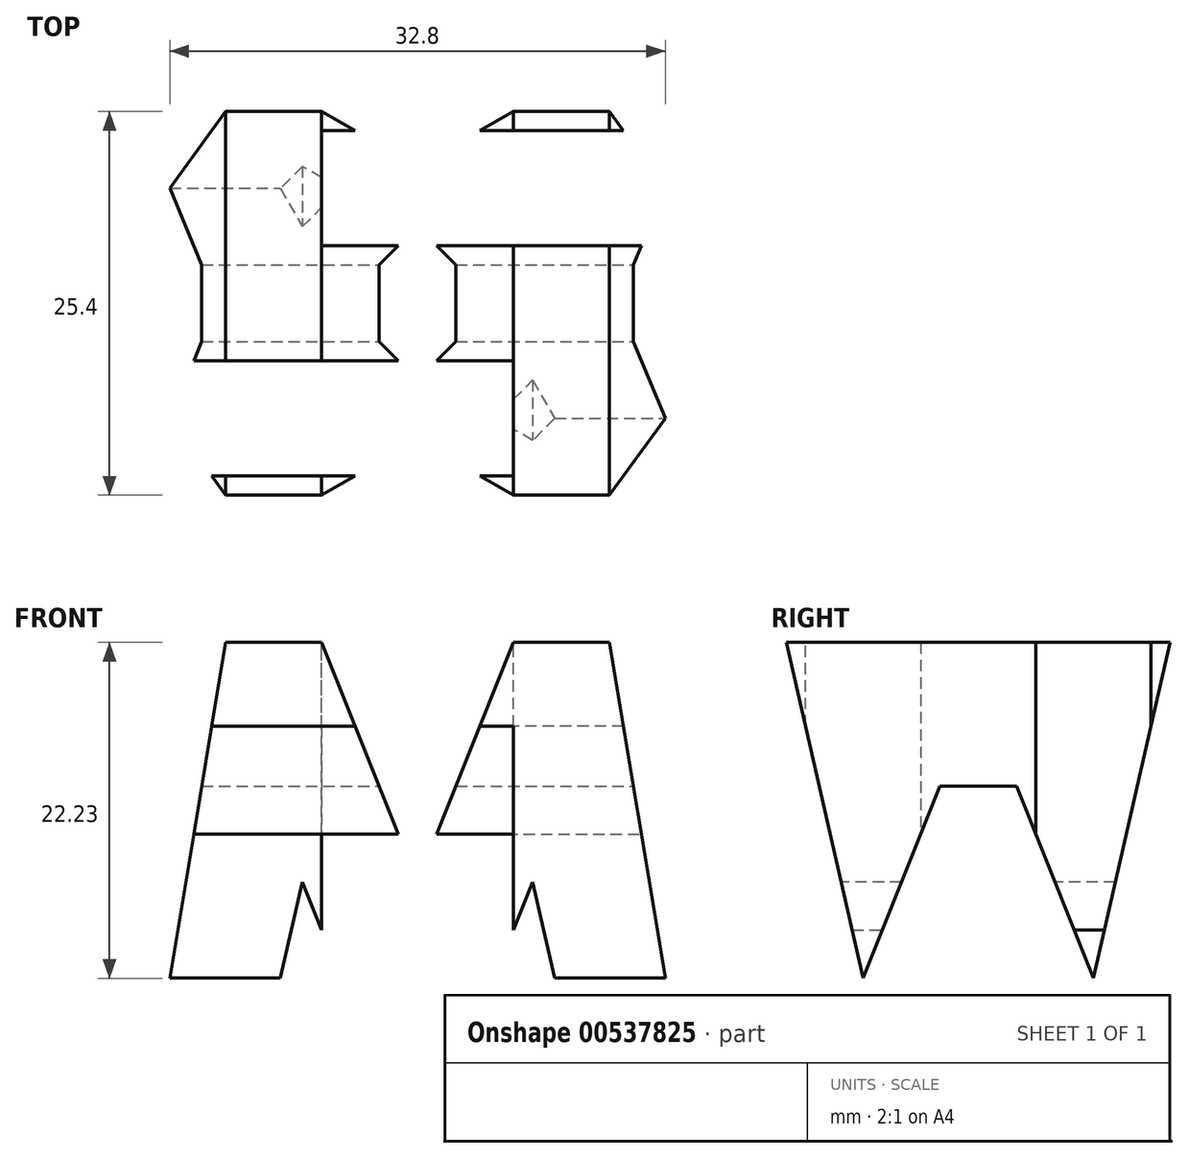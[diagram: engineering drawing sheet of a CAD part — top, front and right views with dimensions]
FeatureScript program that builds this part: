
annotation { "Feature Type Name" : "Feature", "Feature Type Description" : "" }
export const myFeature = defineFeature(function(context is Context, id is Id, definition is map)
    precondition{}
    {
        {
            var Q0;
            Q0=qCreatedBy(makeId("Front.planeOp"),FACE);
            var sketch = newSketch(context, id + "F0", { "sketchPlane" : qUnion([Q0])});
            skLineSegment(sketch, "E0", {"start": v(0, 0) * mm, "end": v(0, 38.1) * mm});
            skLineSegment(sketch, "E1", {"start": v(0, 38.1) * mm, "end": v(38.1, 38.1) * mm});
            skLineSegment(sketch, "E2", {"start": v(38.1, 38.1) * mm, "end": v(38.1, 0) * mm});
            skLineSegment(sketch, "E3", {"start": v(38.1, 0) * mm, "end": v(0, 0) * mm});
            skSolve(sketch);
        }
        {
            var Q0;
            Q0 = qSketchRegion(id + "F0", true);
            extrude(context, id + "F1", {"entities" : qUnion([Q0]), "depth" : 38.1 * mm, "offsetDistance" : 25.4 * mm});
        }
        {
            var Q0;
            Q0=qCreatedBy(makeId("Front.planeOp"),FACE);
            cPlane(context, id + "F2", {"entities" : qUnion([Q0]), "cplaneType" : CPlaneType.OFFSET, "offset" : 38.1 * mm, "width" : 152.4 * mm, "height" : 152.4 * mm});
        }
        {
            var Q0;
            Q0=qCreatedBy(makeId("Right.planeOp"),FACE);
            cPlane(context, id + "F3", {"entities" : qUnion([Q0]), "cplaneType" : CPlaneType.OFFSET, "offset" : 38.1 * mm, "width" : 152.4 * mm, "height" : 152.4 * mm});
        }
        {
            var Q0;
            Q0=qCreatedBy(makeId("Top.planeOp"),FACE);
            cPlane(context, id + "F4", {"entities" : qUnion([Q0]), "cplaneType" : CPlaneType.OFFSET, "offset" : 38.1 * mm, "width" : 152.4 * mm, "height" : 152.4 * mm});
        }
        {
            var Q0;
            Q0=qCreatedBy(id+"F3.planeOp",FACE);
            var sketch = newSketch(context, id + "F5", { "sketchPlane" : qUnion([Q0])});
            skLineSegment(sketch, "E4", {"start": v(0, 0) * mm, "end": v(0, 38.1) * mm});
            skLineSegment(sketch, "E5", {"start": v(0, 38.1) * mm, "end": v(-38.1, 38.1) * mm});
            skLineSegment(sketch, "E6", {"start": v(-38.1, 38.1) * mm, "end": v(-38.1, 0) * mm});
            skLineSegment(sketch, "E7", {"start": v(-38.1, 0) * mm, "end": v(0, 0) * mm});
            skLineSegment(sketch, "E8", {"start": v(-38.1, 38.1) * mm, "end": v(-31.75, 0) * mm});
            skLineSegment(sketch, "E9", {"start": v(-31.75, 0) * mm, "end": v(-25.4, 0) * mm});
            skLineSegment(sketch, "E10", {"start": v(-25.4, 0) * mm, "end": v(-19.05, 15.88) * mm});
            skLineSegment(sketch, "E11", {"start": v(-19.05, 15.88) * mm, "end": v(-12.7, 0) * mm});
            skLineSegment(sketch, "E12", {"start": v(-12.7, 0) * mm, "end": v(-6.35, 0) * mm});
            skLineSegment(sketch, "E13", {"start": v(-6.35, 0) * mm, "end": v(0, 38.1) * mm});
            skLineSegment(sketch, "E14", {"start": v(0, 38.1) * mm, "end": v(-6.35, 38.1) * mm});
            skLineSegment(sketch, "E15", {"start": v(-6.35, 38.1) * mm, "end": v(-11.43, 15.88) * mm});
            skLineSegment(sketch, "E16", {"start": v(-11.43, 15.88) * mm, "end": v(-16.5, 28.58) * mm});
            skLineSegment(sketch, "E17", {"start": v(-16.5, 28.58) * mm, "end": v(-21.59, 28.58) * mm});
            skLineSegment(sketch, "E18", {"start": v(-21.59, 28.58) * mm, "end": v(-26.67, 15.88) * mm});
            skLineSegment(sketch, "E19", {"start": v(-26.67, 15.87) * mm, "end": v(-31.75, 38.1) * mm});
            skLineSegment(sketch, "E20", {"start": v(-31.75, 38.1) * mm, "end": v(-38.1, 38.1) * mm});
            skSolve(sketch);
        }
        {
            var Q0;
            Q0=makeQuery(id+"F5.imprint","IMPRINT",FACE,{"disambiguationData":[TD([[makeQuery(id+"F5.imprint","IMPRINT",EDGE,{"derivedFrom":sQuery(id+"F5.wireOp",EDGE,"E5")}),1.0]])]});
            var Q1;
            {var subQ0=sQuery(id+"F5.wireOp",EDGE,"E4");Q1=makeQuery(id+"F5.imprint","IMPRINT",FACE,{"disambiguationData":[TD([[makeQuery(id+"F5.imprint","IMPRINT",EDGE,{"derivedFrom":subQ0}),1.0]])]});}
            var Q2;
            {var subQ0=sQuery(id+"F5.wireOp",EDGE,"E10");Q2=makeQuery(id+"F5.imprint","IMPRINT",FACE,{"disambiguationData":[TD([[makeQuery(id+"F5.imprint","IMPRINT",EDGE,{"derivedFrom":subQ0}),-1.0]])]});}
            var Q3;
            {var subQ0=sQuery(id+"F5.wireOp",EDGE,"E6");Q3=makeQuery(id+"F5.imprint","IMPRINT",FACE,{"disambiguationData":[TD([[makeQuery(id+"F5.imprint","IMPRINT",EDGE,{"derivedFrom":subQ0}),1.0]])]});}
            extrude(context, id + "F6", {"entities" : qUnion([Q0, Q1, Q2, Q3]), "operationType" : NewBodyOperationType.REMOVE, "oppositeDirection" : true, "depth" : 38.1 * mm, "offsetDistance" : 25.4 * mm});
        }
        {
            var Q0;
            Q0=qCreatedBy(id+"F2.planeOp",FACE);
            var sketch = newSketch(context, id + "F7", { "sketchPlane" : qUnion([Q0])});
            skLineSegment(sketch, "E21", {"start": v(6.35, 38.1) * mm, "end": v(12.7, 38.1) * mm});
            skLineSegment(sketch, "E22", {"start": v(12.7, 38.1) * mm, "end": v(19.05, 22.23) * mm});
            skLineSegment(sketch, "E23", {"start": v(19.05, 22.22) * mm, "end": v(25.4, 38.1) * mm});
            skLineSegment(sketch, "E24", {"start": v(25.4, 38.1) * mm, "end": v(31.75, 38.1) * mm});
            skLineSegment(sketch, "E25", {"start": v(31.75, 38.1) * mm, "end": v(38.1, 0) * mm});
            skLineSegment(sketch, "E26", {"start": v(38.1, 0) * mm, "end": v(31.75, 0) * mm});
            skLineSegment(sketch, "E27", {"start": v(21.6, 9.53) * mm, "end": v(16.51, 9.53) * mm});
            skLineSegment(sketch, "E28", {"start": v(16.51, 9.53) * mm, "end": v(11.43, 22.23) * mm});
            skLineSegment(sketch, "E29", {"start": v(11.43, 22.23) * mm, "end": v(6.35, 0) * mm});
            skLineSegment(sketch, "E30", {"start": v(6.35, 0) * mm, "end": v(0, 0) * mm});
            skLineSegment(sketch, "E31", {"start": v(0, 0) * mm, "end": v(6.35, 38.1) * mm});
            skLineSegment(sketch, "E32.bottom", {"start": v(0, 0) * mm, "end": v(38.1, 0) * mm});
            skLineSegment(sketch, "E32.top", {"start": v(0, 38.1) * mm, "end": v(38.1, 38.1) * mm});
            skLineSegment(sketch, "E32.left", {"start": v(0, 0) * mm, "end": v(0, 38.1) * mm});
            skLineSegment(sketch, "E32.right", {"start": v(38.1, 0) * mm, "end": v(38.1, 38.1) * mm});
            skLineSegment(sketch, "E33", {"start": v(21.6, 9.53) * mm, "end": v(26.67, 22.23) * mm});
            skLineSegment(sketch, "E34", {"start": v(26.67, 22.23) * mm, "end": v(31.75, 0) * mm});
            skSolve(sketch);
        }
        {
            var Q0;
            {var subQ0=sQuery(id+"F7.wireOp",EDGE,"E22");Q0=makeQuery(id+"F7.imprint","IMPRINT",FACE,{"disambiguationData":[TD([[makeQuery(id+"F7.imprint","IMPRINT",EDGE,{"derivedFrom":subQ0}),1.0]])]});}
            var Q1;
            {var subQ0=sQuery(id+"F7.wireOp",EDGE,"E25");Q1=makeQuery(id+"F7.imprint","IMPRINT",FACE,{"disambiguationData":[TD([[makeQuery(id+"F7.imprint","IMPRINT",EDGE,{"derivedFrom":subQ0}),1.0]])]});}
            var Q2;
            Q2=makeQuery(id+"F7.imprint","IMPRINT",FACE,{"disambiguationData":[TD([[makeQuery(id+"F7.imprint","IMPRINT",EDGE,{"derivedFrom":sQuery(id+"F7.wireOp",EDGE,"E27")}),1.0]])]});
            var Q3;
            {var subQ0=sQuery(id+"F7.wireOp",EDGE,"E31");Q3=makeQuery(id+"F7.imprint","IMPRINT",FACE,{"disambiguationData":[TD([[makeQuery(id+"F7.imprint","IMPRINT",EDGE,{"derivedFrom":subQ0}),1.0]])]});}
            extrude(context, id + "F8", {"entities" : qUnion([Q0, Q1, Q2, Q3]), "operationType" : NewBodyOperationType.REMOVE, "oppositeDirection" : true, "depth" : 38.1 * mm, "offsetDistance" : 25.4 * mm});
        }
        {
            var Q0;
            Q0=qCreatedBy(id+"F4.planeOp",FACE);
            var sketch = newSketch(context, id + "F9", { "sketchPlane" : qUnion([Q0])});
            skLineSegment(sketch, "E35", {"start": v(0, 0) * mm, "end": v(0, -38.1) * mm});
            skLineSegment(sketch, "E36", {"start": v(38.1, -38.1) * mm, "end": v(38.1, 0) * mm});
            skLineSegment(sketch, "E37", {"start": v(38.1, 0) * mm, "end": v(0, 0) * mm});
            skLineSegment(sketch, "E38", {"start": v(38.1, -7.62) * mm, "end": v(12.7, -7.62) * mm});
            skLineSegment(sketch, "E39", {"start": v(12.7, -7.62) * mm, "end": v(12.7, -15.24) * mm});
            skLineSegment(sketch, "E40", {"start": v(12.7, -15.24) * mm, "end": v(38.1, -15.24) * mm});
            skLineSegment(sketch, "E41", {"start": v(0, -22.86) * mm, "end": v(25.4, -22.86) * mm});
            skLineSegment(sketch, "E42", {"start": v(25.4, -22.86) * mm, "end": v(25.4, -30.48) * mm});
            skLineSegment(sketch, "E43", {"start": v(25.4, -30.48) * mm, "end": v(0, -30.48) * mm});
            skSolve(sketch);
        }
        {
            var Q0;
            {var subQ0=sQuery(id+"F9.wireOp",EDGE,"E38");Q0=makeQuery(id+"F9.imprint","IMPRINT",FACE,{"disambiguationData":[TD([[makeQuery(id+"F9.imprint","IMPRINT",EDGE,{"derivedFrom":subQ0}),1.0]])]});}
            var Q1;
            {var subQ0=sQuery(id+"F9.wireOp",EDGE,"E41");Q1=makeQuery(id+"F9.imprint","IMPRINT",FACE,{"disambiguationData":[TD([[makeQuery(id+"F9.imprint","IMPRINT",EDGE,{"derivedFrom":subQ0}),-1.0]])]});}
            extrude(context, id + "F10", {"entities" : qUnion([Q0, Q1]), "operationType" : NewBodyOperationType.REMOVE, "oppositeDirection" : true, "depth" : 38.1 * mm, "offsetDistance" : 25.4 * mm});
        }
    });
